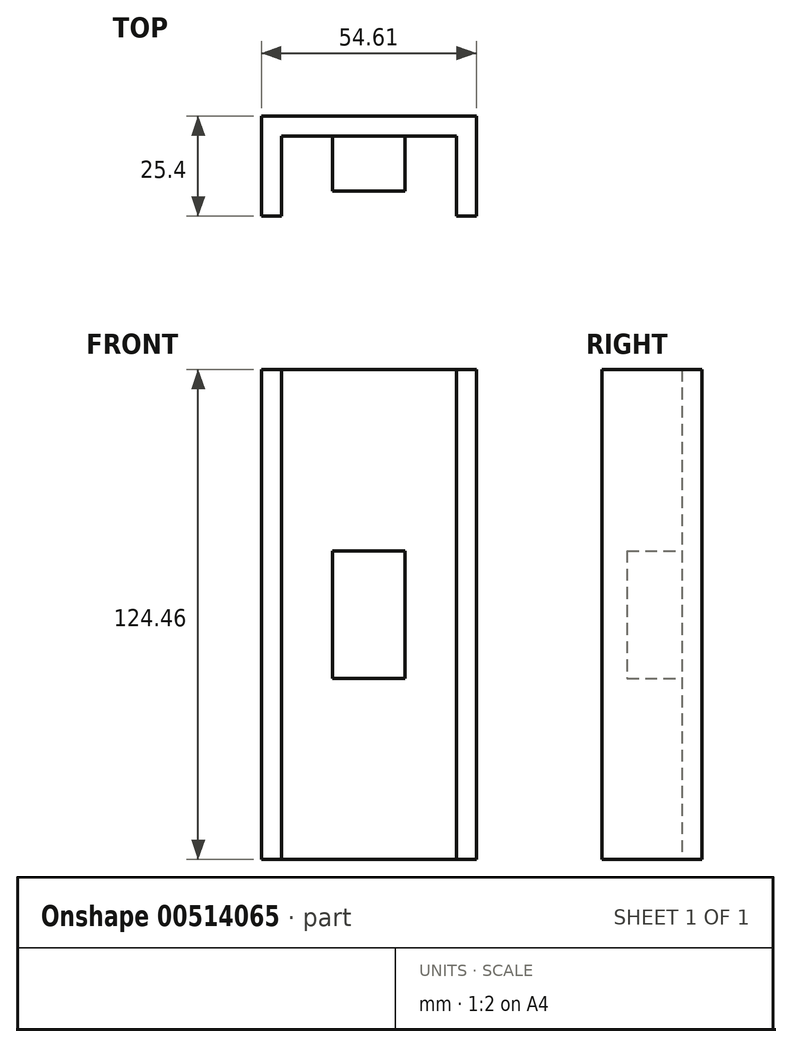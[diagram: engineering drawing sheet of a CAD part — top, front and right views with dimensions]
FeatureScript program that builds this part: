
annotation { "Feature Type Name" : "Feature", "Feature Type Description" : "" }
export const myFeature = defineFeature(function(context is Context, id is Id, definition is map)
    precondition{}
    {
        {
            var Q0;
            Q0=qCreatedBy(makeId("Front.planeOp"),FACE);
            var sketch = newSketch(context, id + "F0", { "sketchPlane" : qUnion([Q0])});
            skLineSegment(sketch, "E0.bottom", {"start": v(-16.72, 62.74) * mm, "end": v(27.73, 62.74) * mm});
            skLineSegment(sketch, "E0.top", {"start": v(-16.72, -61.72) * mm, "end": v(27.73, -61.72) * mm});
            skLineSegment(sketch, "E0.left", {"start": v(-16.72, 62.74) * mm, "end": v(-16.72, -61.72) * mm});
            skLineSegment(sketch, "E0.right", {"start": v(27.73, 62.74) * mm, "end": v(27.73, -61.72) * mm});
            skLineSegment(sketch, "E1.bottom", {"start": v(27.73, 62.74) * mm, "end": v(32.81, 62.74) * mm});
            skLineSegment(sketch, "E1.top", {"start": v(27.73, -61.72) * mm, "end": v(32.81, -61.72) * mm});
            skLineSegment(sketch, "E1.right", {"start": v(32.81, 62.74) * mm, "end": v(32.81, -61.72) * mm});
            skLineSegment(sketch, "E2.bottom", {"start": v(-16.72, 62.74) * mm, "end": v(-21.8, 62.74) * mm});
            skLineSegment(sketch, "E2.top", {"start": v(-16.72, -61.72) * mm, "end": v(-21.8, -61.72) * mm});
            skLineSegment(sketch, "E2.right", {"start": v(-21.8, 62.74) * mm, "end": v(-21.8, -61.72) * mm});
            skLineSegment(sketch, "E3.bottom", {"start": v(-3.7, 16.7) * mm, "end": v(14.72, 16.7) * mm});
            skLineSegment(sketch, "E3.top", {"start": v(-3.7, -15.68) * mm, "end": v(14.72, -15.68) * mm});
            skLineSegment(sketch, "E3.left", {"start": v(-3.7, 16.7) * mm, "end": v(-3.7, -15.68) * mm});
            skLineSegment(sketch, "E3.right", {"start": v(14.72, 16.7) * mm, "end": v(14.72, -15.68) * mm});
            skSolve(sketch);
        }
        {
            var Q0;
            Q0=makeQuery(id+"F0.imprint","IMPRINT",FACE,{"disambiguationData":[TD([[makeQuery(id+"F0.imprint","IMPRINT",EDGE,{"derivedFrom":sQuery(id+"F0.wireOp",EDGE,"E0.bottom")}),-1.0]])]});
            extrude(context, id + "F1", {"entities" : qUnion([Q0]), "depth" : 5.08 * mm, "offsetDistance" : 25.4 * mm});
        }
        {
            var Q0;
            Q0=makeQuery(id+"F0.imprint","IMPRINT",FACE,{"disambiguationData":[TD([[makeQuery(id+"F0.imprint","IMPRINT",EDGE,{"derivedFrom":sQuery(id+"F0.wireOp",EDGE,"E1.bottom")}),-1.0]])]});
            var Q1;
            Q1=makeQuery(id+"F0.imprint","IMPRINT",FACE,{"disambiguationData":[TD([[makeQuery(id+"F0.imprint","IMPRINT",EDGE,{"derivedFrom":sQuery(id+"F0.wireOp",EDGE,"E2.bottom")}),1.0]])]});
            extrude(context, id + "F2", {"entities" : qUnion([Q0, Q1]), "operationType" : NewBodyOperationType.ADD, "depth" : 25.4 * mm, "offsetDistance" : 25.4 * mm});
        }
        {
            var Q0;
            Q0=makeQuery(id+"F0.imprint","IMPRINT",FACE,{"disambiguationData":[TD([[makeQuery(id+"F0.imprint","IMPRINT",EDGE,{"derivedFrom":sQuery(id+"F0.wireOp",EDGE,"E3.bottom")}),-1.0]])]});
            extrude(context, id + "F3", {"entities" : qUnion([Q0]), "operationType" : NewBodyOperationType.ADD, "depth" : 19.05 * mm, "offsetDistance" : 25.4 * mm});
        }
    });
